# Revit family: Weapons Screening Pole
name_source: partatom
category: Security Devices
units: mm (PartAtom-declared; Revit-internal decimal feet)

## family parameters
Always vertical = No
Cut with Voids When Loaded = No
Maintain Annotation Orientation = No
OmniClass Number = 23.85.50.17
OmniClass Title = Communication and Data Processing Equipment
Part Type = Normal
Room Calculation Point = No
Round Connector Dimension = Use Diameter
Shared = No
Work Plane-Based = Yes

## types (3) — shared parameters
Default Elevation = 0' - 0"
Elec Noise Clearance = 5' - 0"
Front Arrow = Yes
Manufacturer = Athena Security
Mech Noise Clearance = 3' - 0"
Pedestal Width = 0' - 10"
URL = https://www.athena-security.com

## per-type parameters (varying)
| type | Lane Plus Pedestal | Lane Width | Lane Width/2 | Pedestal Limits |
| 39" Width | 2' - 5 1/2" | 3' - 3" | 1' - 7 1/2" | 1' - 7 1/2" |
| 30" Width | 2' - 1" | 2' - 6" | 1' - 3" | 1' - 3" |
| Default | 2' - 1" | 2' - 6" | 1' - 3" | 1' - 3" |

## geometry (parser evidence)
native form markers: Sweep x2
no freeform markers — native parametric forms only
